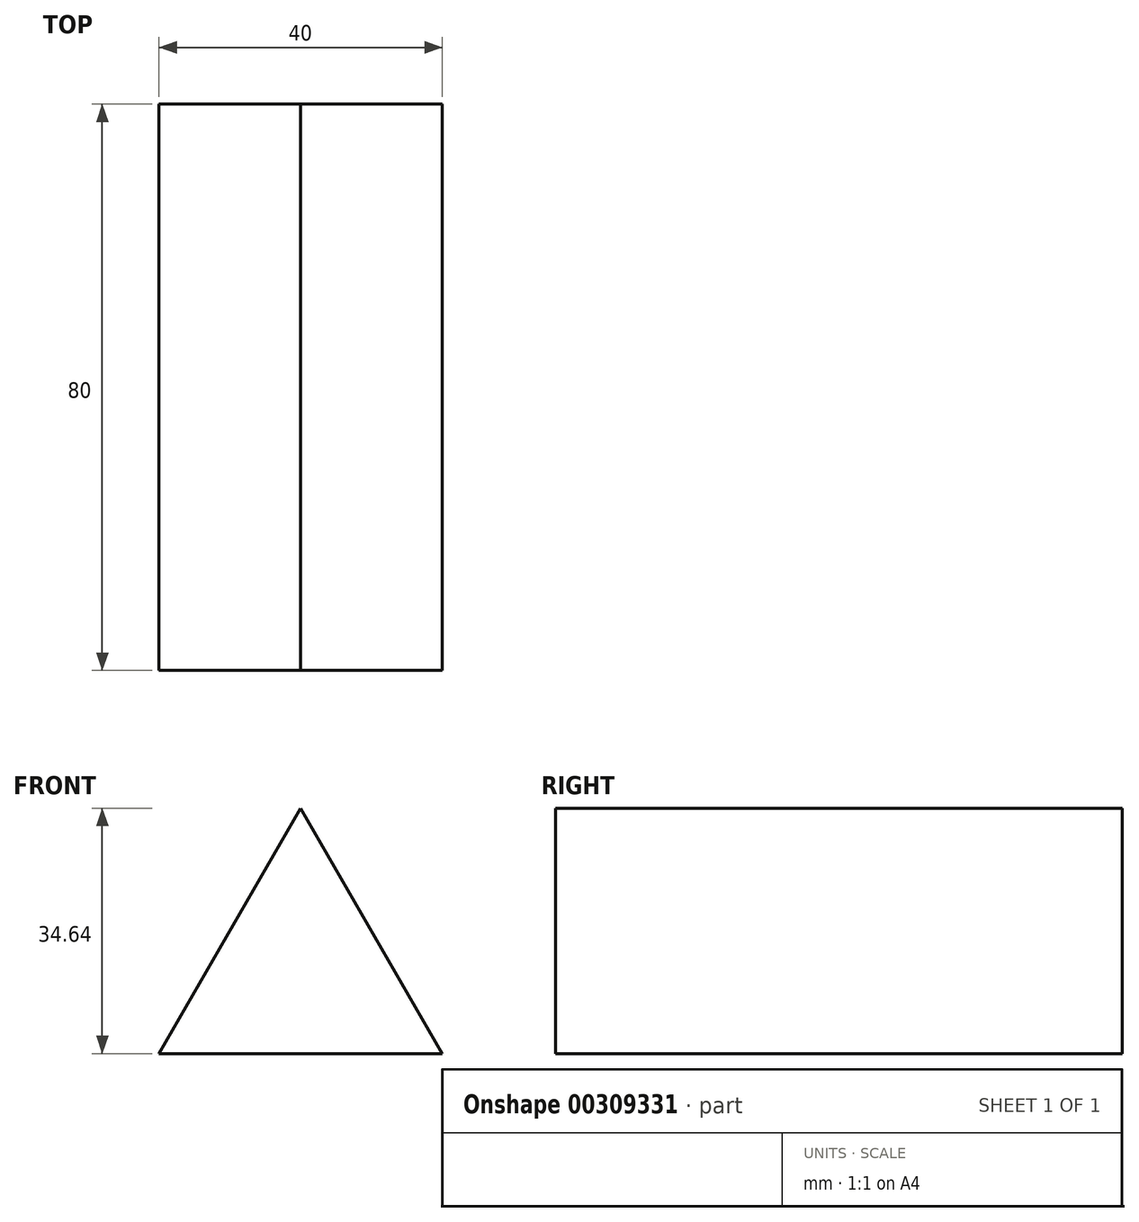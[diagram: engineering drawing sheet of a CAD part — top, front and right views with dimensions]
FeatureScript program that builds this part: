
annotation { "Feature Type Name" : "Feature", "Feature Type Description" : "" }
export const myFeature = defineFeature(function(context is Context, id is Id, definition is map)
    precondition{}
    {
        {
            var Q0;
            Q0=qCreatedBy(makeId("Front.planeOp"),FACE);
            var sketch = newSketch(context, id + "F0", { "sketchPlane" : qUnion([Q0])});
            skLineSegment(sketch, "E0", {"start": v(-20, 0) * mm, "end": v(0, 34.64) * mm});
            skLineSegment(sketch, "E1", {"start": v(-20, 0) * mm, "end": v(20, 0) * mm});
            skLineSegment(sketch, "E2", {"start": v(0, 34.64) * mm, "end": v(20, 0) * mm});
            skSolve(sketch);
        }
        {
            var Q0;
            Q0 = qSketchRegion(id + "F0", true);
            extrude(context, id + "F1", {"entities" : qUnion([Q0]), "depth" : 80 * mm});
        }
    });
